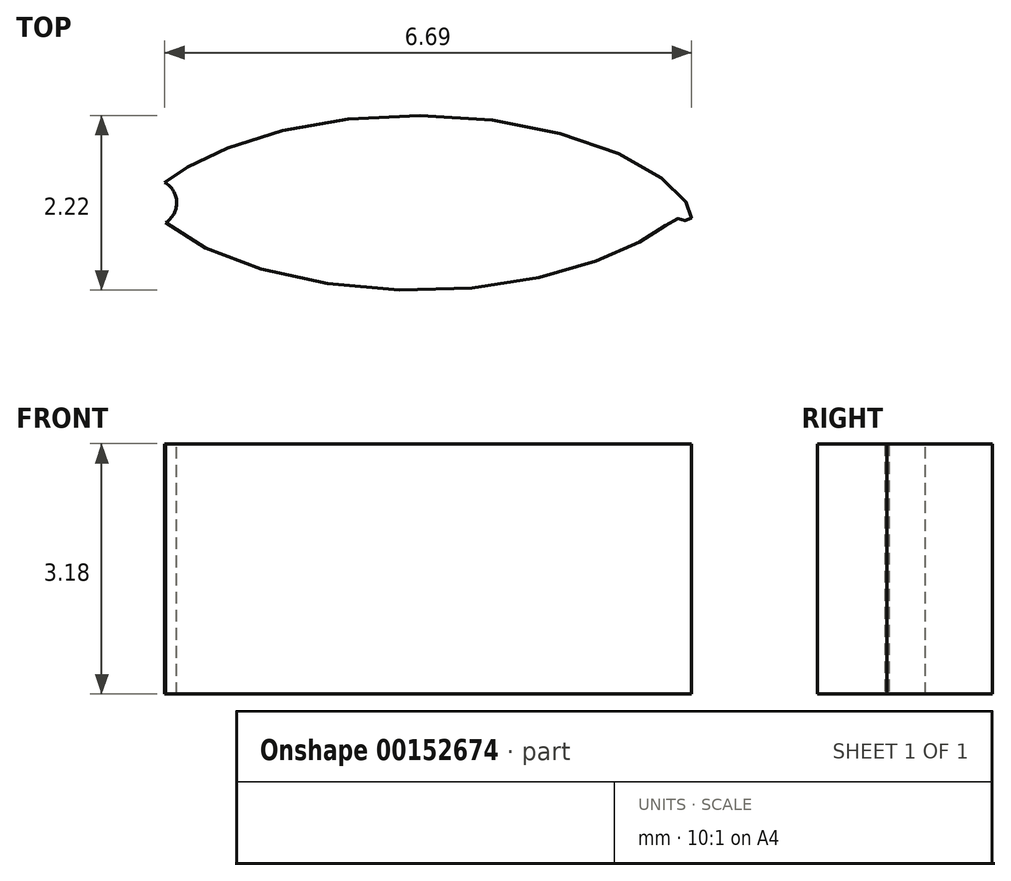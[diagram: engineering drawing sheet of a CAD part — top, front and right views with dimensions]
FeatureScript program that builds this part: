
annotation { "Feature Type Name" : "Feature", "Feature Type Description" : "" }
export const myFeature = defineFeature(function(context is Context, id is Id, definition is map)
    precondition{}
    {
        {
            var Q0;
            Q0=qCreatedBy(makeId("Top.planeOp"),FACE);
            var sketch = newSketch(context, id + "F0", { "sketchPlane" : qUnion([Q0])});
            skLineSegment(sketch, "E0", {"start": v(0, 0) * mm, "end": v(-4.83, 0) * mm, "construction": true});
            skLineSegment(sketch, "E1", {"start": v(0, 0) * mm, "end": v(0, 2.54) * mm, "construction": true});
            skEllipse(sketch, "E2", {"center": v(0, 0) * mm, "majorRadius": 4.83 * mm, "minorRadius": 2.54 * mm, "majorAxis": v(1, 0)});
            skSolve(sketch);
        }
        {
            var Q0;
            Q0 = qSketchRegion(id + "F0", true);
            extrude(context, id + "F1", {"entities" : qUnion([Q0]), "depth" : 3.17 * mm});
        }
        {
            var Q0;
            Q0=makeQuery(id+"F1.opExtrude","CAP_FACE",FACE,{"disambiguationData":[OSD([sQuery(id+"F0.wireOp",EDGE,"E2")])],"isStart":false});
            var sketch = newSketch(context, id + "F2", { "sketchPlane" : qUnion([Q0])});
            skLineSegment(sketch, "E3", {"start": v(0, 0) * mm, "end": v(-4.83, 0) * mm, "construction": true});
            skLineSegment(sketch, "E4", {"start": v(0, 0) * mm, "end": v(-4.62, 0.74) * mm, "construction": true});
            skEllipse(sketch, "E5", {"center": v(0, 0) * mm, "majorRadius": 4.83 * mm, "minorRadius": 2.54 * mm, "majorAxis": v(1, 0)});
            skLineSegment(sketch, "E6", {"start": v(-4.47, -0.96) * mm, "end": v(-3.2, -0.26) * mm});
            skLineSegment(sketch, "E7", {"start": v(-4.47, 0.96) * mm, "end": v(-3.2, 0.26) * mm});
            skArc(sketch, "E8", {"start": v(-3.2, -0.26) * mm, "mid": v(-3.05, 0) * mm, "end": v(-3.2, 0.26) * mm});
            skPoint(sketch, "E9", {"position": v(-3.83, 0.61) * mm});
            skLineSegment(sketch, "E10", {"start": v(-3.83, -0.61) * mm, "end": v(-3.83, 0) * mm, "construction": true});
            skLineSegment(sketch, "E11", {"start": v(-3.83, 0) * mm, "end": v(-3.83, 0.61) * mm, "construction": true});
            skSolve(sketch);
        }
        {
            var Q0;
            {var subQ0=sQuery(id+"F2.wireOp",EDGE,"E6");Q0=makeQuery(id+"F2.imprint","IMPRINT",FACE,{"disambiguationData":[TD([[makeQuery(id+"F2.imprint","IMPRINT",EDGE,{"derivedFrom":subQ0}),1.0]])]});}
            var Q1;
            Q1=makeQuery(id+"F1.opExtrude","CAP_FACE",FACE,{"disambiguationData":[OSD([sQuery(id+"F0.wireOp",EDGE,"E2")])],"isStart":true});
            extrude(context, id + "F3", {"entities" : qUnion([Q0]), "operationType" : NewBodyOperationType.REMOVE, "endBound" : BoundingType.UP_TO_SURFACE, "oppositeDirection" : true, "endBoundEntityFace" : qUnion([Q1]), "depth" : 25.4 * mm});
        }
        {
            var Q0;
            Q0=makeQuery(id+"F3.boolean.opBoolean","COPY",FACE,{"derivedFrom":makeQuery(id+"F3.opExtrude","SWEPT_FACE",FACE,{"disambiguationData":[OSD([sQuery(id+"F2.wireOp",EDGE,"E7")])]})});
            var Q1;
            Q1=makeQuery(id+"F1.opExtrude","CAP_EDGE",EDGE,{"disambiguationData":[OSD([sQuery(id+"F0.wireOp",EDGE,"E2")])],"isStart":false});
            sweep(context, id + "F4", {"operationType" : NewBodyOperationType.REMOVE, "profiles" : qUnion([Q0]), "path" : qUnion([Q1])});
        }
    });
